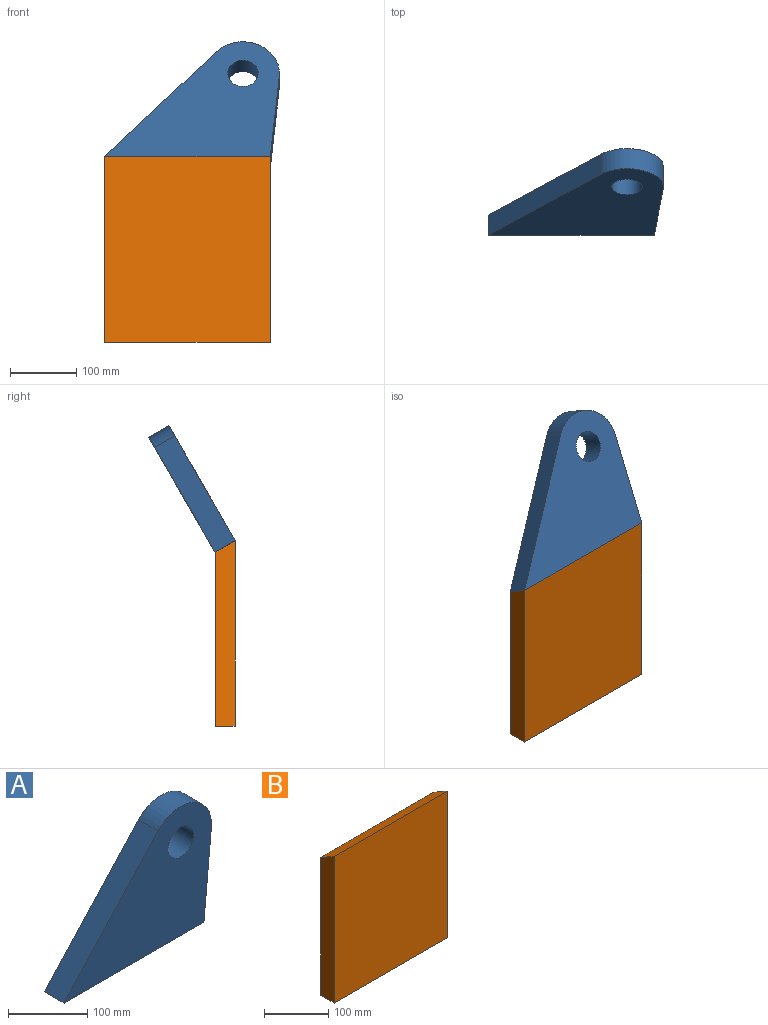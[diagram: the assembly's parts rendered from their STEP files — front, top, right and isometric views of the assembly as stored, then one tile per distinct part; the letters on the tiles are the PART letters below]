
ASSEMBLY  parts=2 mates=1
PART A: 7 faces, bbox 263.7x35x200 mm
  f0: plane 250x35mm, normal (0,0,-1), area 8750mm2, adj f1,f3,f5,f6
  f1: plane 139.73x35mm, normal (1,0,-0.1), area 4913mm2, adj f0,f2,f5,f6
  f2: cylinder r=55mm len=95.41mm, axis (0,1,0), area 4797.4mm2, adj f1,f3,f5,f6
  f3: plane 182.31x168.3mm, normal (-0.73,0,0.68), area 8684.1mm2, adj f0,f2,f5,f6
  f4: cylinder r=23mm len=46mm, axis (0,1,0), area 5058mm2, adj f5,f6
  f5: plane 263.72x200mm, normal (0,-1,0), area 30916mm2, adj f0,f1,f2,f3,f4
  f6: plane 263.72x200mm, normal (0,1,0), area 30916mm2, adj f0,f1,f2,f3,f4
PART B: 6 faces, bbox 250x30x280 mm
  f0: plane 280x30mm, normal (1,0,0), area 8140.2mm2, adj f2,f3,f4,f5
  f1: plane 280x30mm, normal (-1,0,0), area 8140.2mm2, adj f2,f3,f4,f5
  f2: plane 250x30mm, normal (0,0,-1), area 7500mm2, adj f0,f1,f3,f4
  f3: plane 280x250mm, normal (0,-1,0), area 70000mm2, adj f0,f1,f2,f5
  f4: plane 262.68x250mm, normal (0,1,0), area 65669.9mm2, adj f0,f1,f2,f5
  f5: plane 250x30mm, normal (0,0.5,0.87), area 8660.3mm2, adj f0,f1,f3,f4
PLACE A rot(axis=(-1,0,0),30deg) t=(-59.18,-58.57,50.25)mm
PLACE B t=(-24.28,-113.53,-167.27)mm
MATE fastened A.f0 <-> B.f5  axis (0,-0.5,-0.87) through (-24.28,-128.53,-35.93)mm
